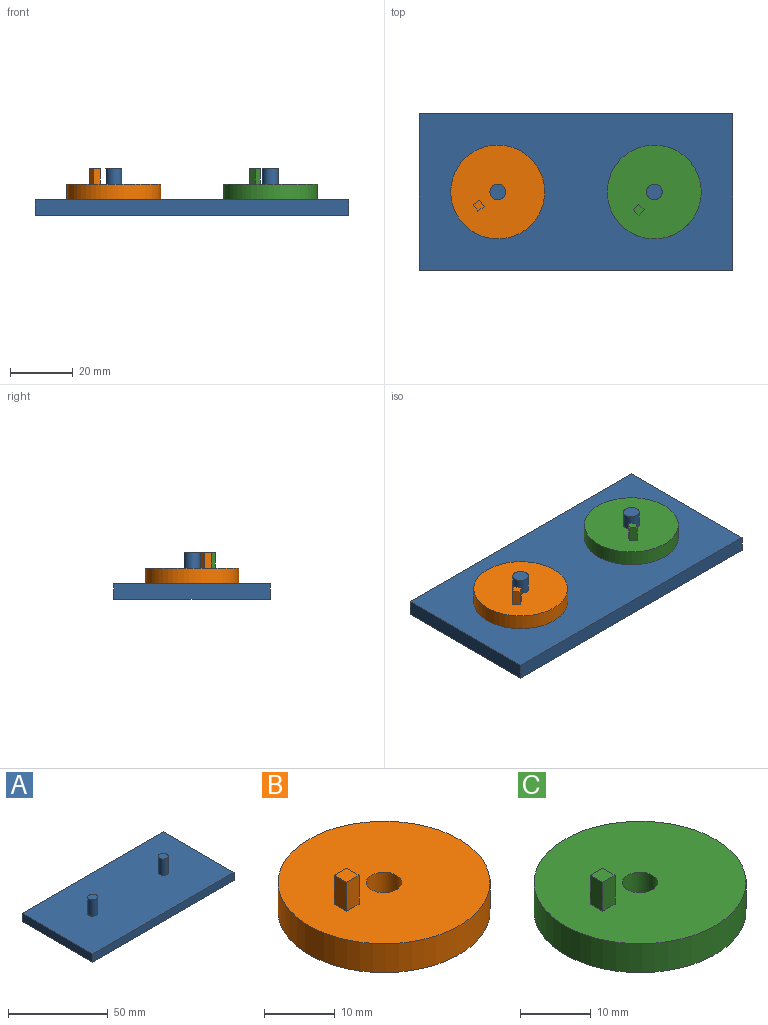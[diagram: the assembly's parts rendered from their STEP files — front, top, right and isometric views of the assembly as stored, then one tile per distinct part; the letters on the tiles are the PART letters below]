
ASSEMBLY  parts=3 mates=2
PART A: 10 faces, bbox 100x50x15 mm
  f0: plane 100x5mm, normal (0,-1,0), area 500mm2, adj f1,f3,f4,f5
  f1: plane 50x5mm, normal (1,0,0), area 250mm2, adj f0,f2,f4,f5
  f2: plane 100x5mm, normal (0,1,0), area 500mm2, adj f1,f3,f4,f5
  f3: plane 50x5mm, normal (-1,0,0), area 250mm2, adj f0,f2,f4,f5
  f4: plane 100x50mm, normal (0,0,1), area 4960.7mm2, adj f0,f1,f2,f3,f6,f8
  f5: plane 100x50mm, normal (0,0,-1), area 5000mm2, adj f0,f1,f2,f3
  f6: cylinder r=2.5mm len=10mm, axis (0,0,-1), area 157.1mm2, adj f4,f7
  f7: plane 5x5mm, normal (0,0,1), area 19.6mm2, adj f6
  f8: cylinder r=2.5mm len=10mm, axis (0,0,-1), area 157.1mm2, adj f4,f9
  f9: plane 5x5mm, normal (0,0,1), area 19.6mm2, adj f8
PART B: 9 faces, bbox 30x30x10 mm
  f0: plane 30x30mm, normal (0,0,1), area 681mm2, adj f1,f2,f4,f5,f6,f7
  f1: cylinder r=2.5mm len=5mm, axis (0,0,-1), area 78.5mm2, adj f0,f3
  f2: cylinder r=15mm len=30mm, axis (0,0,-1), area 471.2mm2, adj f0,f3
  f3: plane 30x30mm, normal (0,0,-1), area 687.2mm2, adj f1,f2
  f4: plane 5x2.5mm, normal (0,-1,0), area 12.5mm2, adj f0,f5,f7,f8
  f5: plane 5x2.5mm, normal (1,0,0), area 12.5mm2, adj f0,f4,f6,f8
  f6: plane 5x2.5mm, normal (0,1,0), area 12.5mm2, adj f0,f5,f7,f8
  f7: plane 5x2.5mm, normal (-1,0,0), area 12.5mm2, adj f0,f4,f6,f8
  f8: plane 2.5x2.5mm, normal (0,0,1), area 6.3mm2, adj f4,f5,f6,f7
PART C: 9 faces, bbox 30x30x10 mm
  f0: plane 30x30mm, normal (0,0,1), area 681mm2, adj f1,f2,f4,f5,f6,f7
  f1: cylinder r=2.5mm len=5mm, axis (0,0,-1), area 78.5mm2, adj f0,f3
  f2: cylinder r=15mm len=30mm, axis (0,0,-1), area 471.2mm2, adj f0,f3
  f3: plane 30x30mm, normal (0,0,-1), area 687.2mm2, adj f1,f2
  f4: plane 5x2.5mm, normal (0,-1,0), area 12.5mm2, adj f0,f5,f7,f8
  f5: plane 5x2.5mm, normal (1,0,0), area 12.5mm2, adj f0,f4,f6,f8
  f6: plane 5x2.5mm, normal (0,1,0), area 12.5mm2, adj f0,f5,f7,f8
  f7: plane 5x2.5mm, normal (-1,0,0), area 12.5mm2, adj f0,f4,f6,f8
  f8: plane 2.5x2.5mm, normal (0,0,1), area 6.2mm2, adj f4,f5,f6,f7
PLACE A t=(6.89,-35.33,-17.68)mm fixed
PLACE B rot(axis=(0,0,1),35.7deg) t=(2.2,-20.74,-17.68)mm
PLACE C rot(axis=(0,0,1),48.8deg) t=(15.41,-54.13,-17.68)mm
MATE revolute B.f1 <-> A.f6  axis (0,0,-1) through (-18.11,-35.33,-12.68)mm
MATE revolute C.f2 <-> A.f8  axis (0,0,-1) through (31.89,-35.33,-12.68)mm
